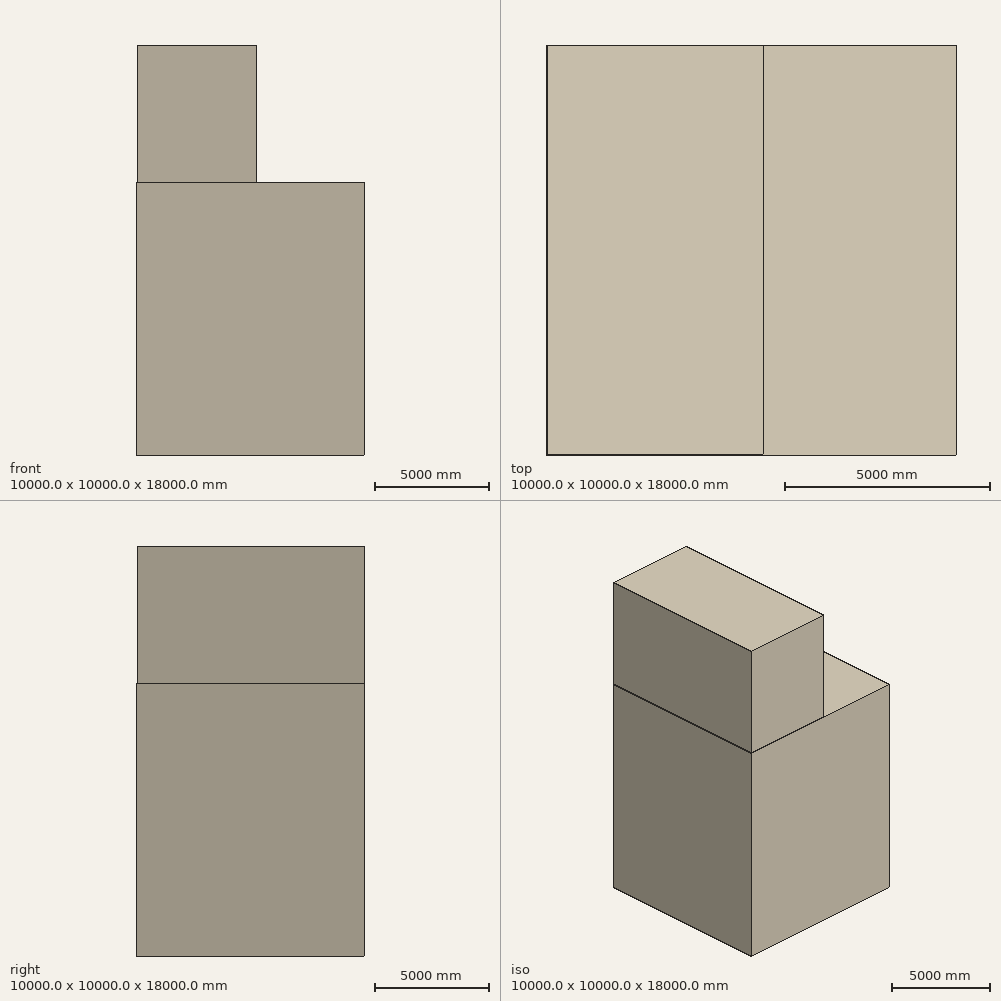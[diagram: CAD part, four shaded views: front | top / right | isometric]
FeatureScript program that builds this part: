
annotation { "Feature Type Name" : "Feature", "Feature Type Description" : "" }
export const myFeature = defineFeature(function(context is Context, id is Id, definition is map)
    precondition{}
    {
        {
            var Q0;
            Q0=qCreatedBy(makeId("Top.planeOp"),FACE);
            var sketch = newSketch(context, id + "F0", { "sketchPlane" : qUnion([Q0])});
            skLineSegment(sketch, "E0.bottom", {"start": v(-34.22, 9963.93) * mm, "end": v(9965.78, 9963.93) * mm});
            skLineSegment(sketch, "E0.top", {"start": v(-34.22, -36.07) * mm, "end": v(9965.78, -36.07) * mm});
            skLineSegment(sketch, "E0.left", {"start": v(-34.22, 9963.93) * mm, "end": v(-34.22, -36.07) * mm});
            skLineSegment(sketch, "E0.right", {"start": v(9965.78, 9963.93) * mm, "end": v(9965.78, -36.07) * mm});
            skSolve(sketch);
        }
        {
            var Q0;
            Q0=makeQuery(id+"F0.imprint","IMPRINT",FACE,{"disambiguationData":[TD([[makeQuery(id+"F0.imprint","IMPRINT",EDGE,{"derivedFrom":sQuery(id+"F0.wireOp",EDGE,"E0.bottom")}),-1.0]])]});
            extrude(context, id + "F1", {"entities" : qUnion([Q0]), "depth" : 12000 * mm, "offsetDistance" : 25 * mm});
        }
        {
            var Q0;
            Q0=makeQuery(id+"F1.opExtrude","CAP_FACE",FACE,{"disambiguationData":[OSD([sQuery(id+"F0.wireOp",EDGE,"E0.bottom"),sQuery(id+"F0.wireOp",EDGE,"E0.top"),sQuery(id+"F0.wireOp",EDGE,"E0.left"),sQuery(id+"F0.wireOp",EDGE,"E0.right")])],"isStart":false});
            var sketch = newSketch(context, id + "F2", { "sketchPlane" : qUnion([Q0])});
            skSolve(sketch);
        }
        {
            var Q0;
            Q0=makeQuery(id+"F2.imprint","IMPRINT",FACE,{"disambiguationData":[TD([[makeQuery(id+"F2.imprint","IMPRINT",EDGE,{"derivedFrom":makeQuery(id+"F1.opExtrude","CAP_EDGE",EDGE,{"disambiguationData":[OSD([sQuery(id+"F0.wireOp",EDGE,"E0.bottom")])],"isStart":false})}),-1.0]])]});
            var sketch = newSketch(context, id + "F3", { "sketchPlane" : qUnion([Q0])});
            skLineSegment(sketch, "E1.bottom", {"start": v(0, 0) * mm, "end": v(5250, 0) * mm});
            skLineSegment(sketch, "E1.top", {"start": v(0, 10000) * mm, "end": v(5250, 10000) * mm});
            skLineSegment(sketch, "E1.left", {"start": v(0, 0) * mm, "end": v(0, 10000) * mm});
            skLineSegment(sketch, "E1.right", {"start": v(5250, 0) * mm, "end": v(5250, 10000) * mm});
            skSolve(sketch);
        }
        {
            var Q0;
            Q0=makeQuery(id+"F1.opExtrude","SWEPT_FACE",FACE,{"disambiguationData":[OSD([sQuery(id+"F0.wireOp",EDGE,"E0.left")])]});
            var sketch = newSketch(context, id + "F4", { "sketchPlane" : qUnion([Q0])});
            skLineSegment(sketch, "E2.bottom", {"start": v(36.07, 12000) * mm, "end": v(-9963.93, 12000) * mm});
            skLineSegment(sketch, "E2.top", {"start": v(36.07, 18000) * mm, "end": v(-9963.93, 18000) * mm});
            skLineSegment(sketch, "E2.left", {"start": v(36.07, 12000) * mm, "end": v(36.07, 18000) * mm});
            skLineSegment(sketch, "E2.right", {"start": v(-9963.93, 12000) * mm, "end": v(-9963.93, 18000) * mm});
            skLineSegment(sketch, "E3.bottom", {"start": v(36.07, 12000) * mm, "end": v(-4963.93, 12000) * mm});
            skLineSegment(sketch, "E3.top", {"start": v(36.07, 18000) * mm, "end": v(-4963.93, 18000) * mm});
            skLineSegment(sketch, "E3.right", {"start": v(-4963.93, 12000) * mm, "end": v(-4963.93, 18000) * mm});
            skSolve(sketch);
        }
        {
            var Q0;
            {var subQ0=sQuery(id+"F3.wireOp",EDGE,"E1.bottom");Q0=makeQuery(id+"F3.imprint","IMPRINT",FACE,{"disambiguationData":[TD([[makeQuery(id+"F3.imprint","IMPRINT",EDGE,{"derivedFrom":subQ0}),1.0]])]});}
            extrude(context, id + "F5", {"entities" : qUnion([Q0]), "operationType" : NewBodyOperationType.ADD, "depth" : 6000 * mm, "offsetDistance" : 25 * mm});
        }
        {
            var Q0;
            Q0=makeQuery(id+"F4.imprint","IMPRINT",FACE,{"disambiguationData":[TD([[makeQuery(id+"F4.imprint","IMPRINT",EDGE,{"derivedFrom":sQuery(id+"F4.wireOp",EDGE,"E3.bottom")}),1.0]])]});
            var sketch = newSketch(context, id + "F6", { "sketchPlane" : qUnion([Q0])});
            skLineSegment(sketch, "E4", {"start": v(-4973.48, 18078.22) * mm, "end": v(0, 11982.08) * mm});
            skSolve(sketch);
        }
        {
            var Q0;
            {var subQ5=makeQuery(id+"F4.imprint","IMPRINT",EDGE,{"derivedFrom":sQuery(id+"F4.wireOp",EDGE,"E2.left")});Q0=makeQuery(id+"F6.imprint","IMPRINT",FACE,{"disambiguationData":[TD([[makeQuery(id+"F6.imprint","IMPRINT",EDGE,{"derivedFrom":subQ5}),1.0]])]});}
            var Q1;
            Q1=makeQuery(id+"F5.opExtrude","CAP_FACE",FACE,{"disambiguationData":[OSD([sQuery(id+"F0.wireOp",EDGE,"E0.bottom"),sQuery(id+"F3.wireOp",EDGE,"E1.bottom"),sQuery(id+"F3.wireOp",EDGE,"E1.left"),sQuery(id+"F3.wireOp",EDGE,"E1.right")])],"isStart":false});
            extrude(context, id + "F7", {"entities" : qUnion([Q0, Q1]), "operationType" : NewBodyOperationType.ADD, "oppositeDirection" : true, "depth" : 5250 * mm, "offsetDistance" : 25 * mm});
        }
    });
